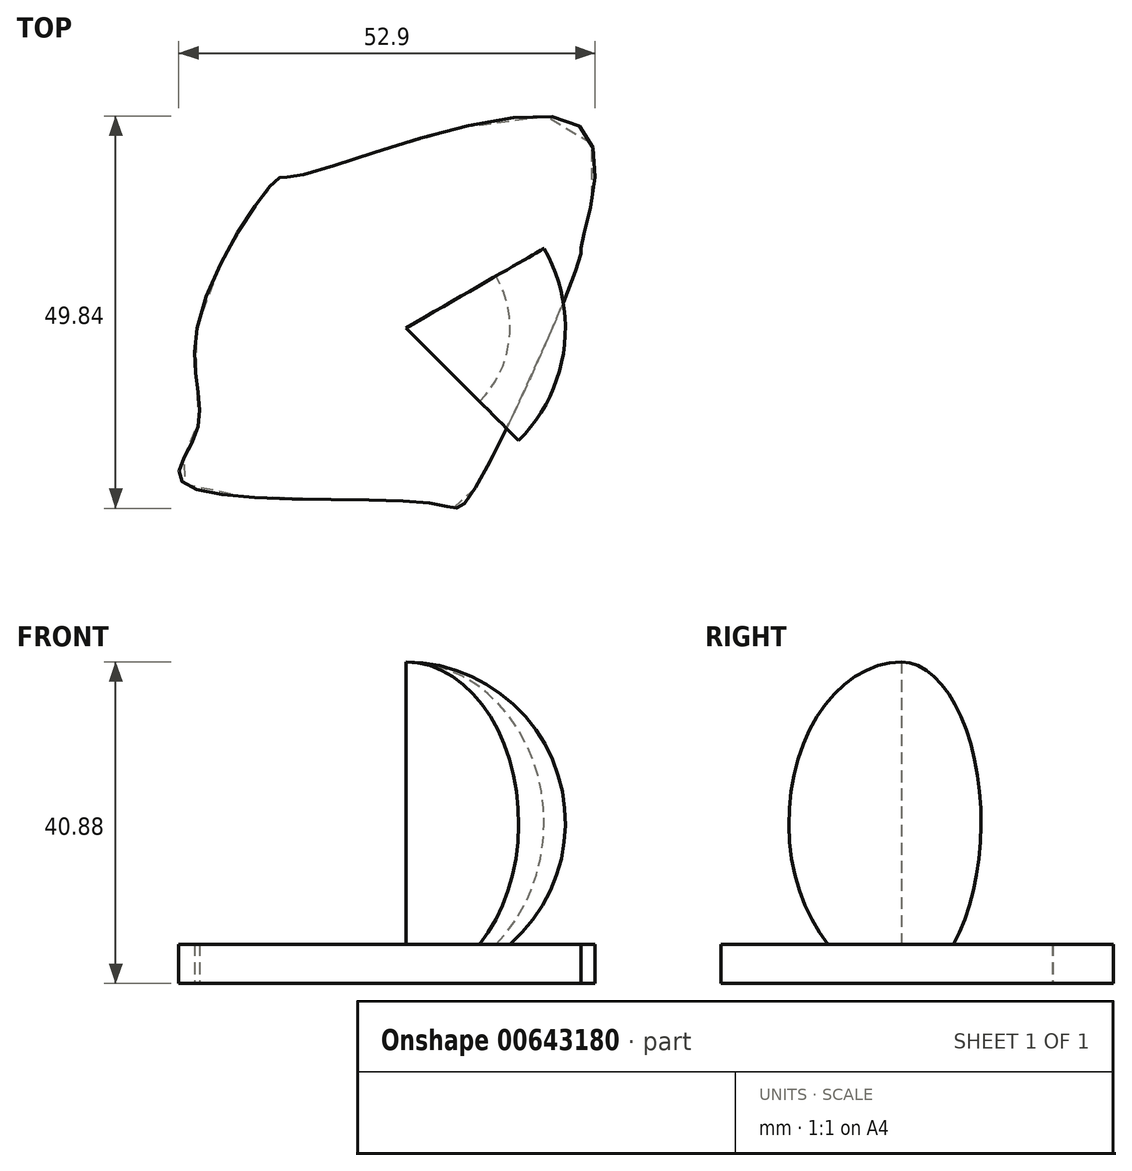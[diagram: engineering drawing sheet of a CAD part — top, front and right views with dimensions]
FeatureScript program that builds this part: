
annotation { "Feature Type Name" : "Feature", "Feature Type Description" : "" }
export const myFeature = defineFeature(function(context is Context, id is Id, definition is map)
    precondition{}
    {
        {
            var Q0;
            Q0=qCreatedBy(makeId("Top.planeOp"),FACE);
            var sketch = newSketch(context, id + "F0", { "sketchPlane" : qUnion([Q0])});
            skFitSpline(sketch, "E0", {"points": [v(-26.56, 0) * mm, v(-16.3, 18.95) * mm, v(-14.13, 19.26) * mm, v(22.21, 25.47) * mm, v(22.21, 10.25) * mm, v(22.21, 9.32) * mm, v(7.61, -22.06) * mm, v(3.88, -22.37) * mm, v(-28.42, -19.57) * mm, v(-26.56, -13.05) * mm, v(-26.56, 0) * mm]});
            skSolve(sketch);
        }
        {
            var Q0;
            Q0=makeQuery(id+"F0.imprint","IMPRINT",FACE,{"disambiguationData":[TD([[makeQuery(id+"F0.imprint","IMPRINT",EDGE,{"derivedFrom":sQuery(id+"F0.wireOp",EDGE,"E0")}),-1.0]])]});
            extrude(context, id + "F1", {"entities" : qUnion([Q0]), "depth" : 5 * mm, "offsetDistance" : 25 * mm});
        }
        {
            var Q0;
            Q0=qCreatedBy(makeId("Front.planeOp"),FACE);
            var sketch = newSketch(context, id + "F2", { "sketchPlane" : qUnion([Q0])});
            skLineSegment(sketch, "E1", {"start": v(0, 40.88) * mm, "end": v(0, 0) * mm});
            skArc(sketch, "E2", {"start": v(0, 0) * mm, "mid": v(20.23, 20.44) * mm, "end": v(0, 40.88) * mm});
            skSolve(sketch);
        }
        {
            var Q0;
            Q0=makeQuery(id+"F2.imprint","IMPRINT",FACE,{"disambiguationData":[TD([[makeQuery(id+"F2.imprint","IMPRINT",EDGE,{"derivedFrom":sQuery(id+"F2.wireOp",EDGE,"E1")}),1.0]])]});
            var Q1;
            Q1=sQuery(id+"F2.wireOp",EDGE,"E1");
            revolve(context, id + "F3", {"operationType" : NewBodyOperationType.ADD, "surfaceOperationType" : NewSurfaceOperationType.NEW, "entities" : qUnion([Q0]), "axis" : qUnion([Q1]), "revolveType" : RevolveType.TWO_DIRECTIONS, "angle" : 45 * degree, "angleBack" : 330 * degree});
        }
    });
